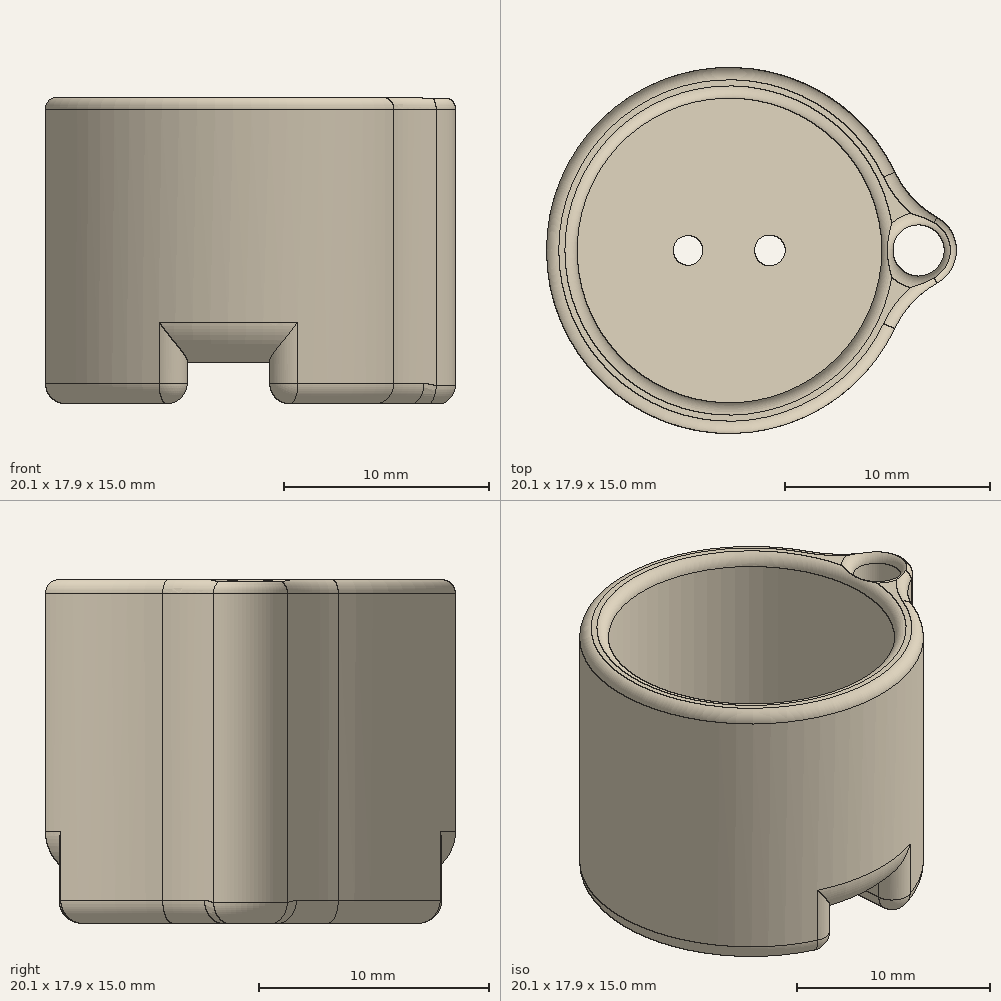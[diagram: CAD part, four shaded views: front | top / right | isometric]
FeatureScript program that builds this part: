
annotation { "Feature Type Name" : "Feature", "Feature Type Description" : "" }
export const myFeature = defineFeature(function(context is Context, id is Id, definition is map)
    precondition{}
    {
        {
            var Q0;
            Q0=qCreatedBy(makeId("Top.planeOp"),FACE);
            var sketch = newSketch(context, id + "F0", { "sketchPlane" : qUnion([Q0])});
            skCircle(sketch, "E0", {"center": v(0, 0) * mm, "radius": 7.45 * mm});
            skCircle(sketch, "E1", {"center": v(9.25, 0) * mm, "radius": 1.25 * mm});
            skArc(sketch, "E2.0", {"start": v(8.09, 3.83) * mm, "mid": v(-8.95, 0) * mm, "end": v(8.09, -3.83) * mm});
            skArc(sketch, "E3.0", {"start": v(10.16, -1.61) * mm, "mid": v(11.1, 0) * mm, "end": v(10.16, 1.61) * mm});
            skPoint(sketch, "E4.visualSharp", {"position": v(8.77, 1.79) * mm});
            skArc(sketch, "E4.filletArc", {"start": v(8.09, 3.83) * mm, "mid": v(8.95, 2.56) * mm, "end": v(10.16, 1.61) * mm});
            skPoint(sketch, "E5.visualSharp", {"position": v(8.77, -1.79) * mm});
            skArc(sketch, "E5.filletArc", {"start": v(10.16, -1.61) * mm, "mid": v(8.95, -2.56) * mm, "end": v(8.09, -3.83) * mm});
            skSolve(sketch);
        }
        {
            var Q0;
            Q0=makeQuery(id+"F0.imprint","IMPRINT",FACE,{"disambiguationData":[TD([[makeQuery(id+"F0.imprint","IMPRINT",EDGE,{"derivedFrom":sQuery(id+"F0.wireOp",EDGE,"E2.0")}),1.0]])]});
            extrude(context, id + "F1", {"entities" : qUnion([Q0]), "depth" : 15 * mm});
        }
        {
            var Q0;
            Q0=makeQuery(id+"F0.imprint","IMPRINT",FACE,{"disambiguationData":[TD([[makeQuery(id+"F0.imprint","IMPRINT",EDGE,{"derivedFrom":sQuery(id+"F0.wireOp",EDGE,"E0")}),1.0]])]});
            extrude(context, id + "F2", {"entities" : qUnion([Q0]), "operationType" : NewBodyOperationType.ADD, "depth" : 3 * mm});
        }
        {
            var Q0;
            Q0=makeQuery(id+"F1.opExtrude","CAP_FACE",FACE,{"disambiguationData":[OSD([sQuery(id+"F0.wireOp",EDGE,"E0"),sQuery(id+"F0.wireOp",EDGE,"E1"),sQuery(id+"F0.wireOp",EDGE,"E2.0"),sQuery(id+"F0.wireOp",EDGE,"E3.0"),sQuery(id+"F0.wireOp",EDGE,"E4.filletArc"),sQuery(id+"F0.wireOp",EDGE,"E5.filletArc")])],"isStart":false});
            fillet(context, id + "F3", {"entities" : qUnion([Q0]), "radius" : 0.6 * mm, "tangentPropagation" : true, "allowEdgeOverflow" : false});
        }
        {
            var Q0;
            Q0=makeQuery(id+"F0.imprint","IMPRINT",FACE,{"disambiguationData":[TD([[makeQuery(id+"F0.imprint","IMPRINT",EDGE,{"derivedFrom":sQuery(id+"F0.wireOp",EDGE,"E0")}),1.0]])]});
            var sketch = newSketch(context, id + "F4", { "sketchPlane" : qUnion([Q0])});
            skLineSegment(sketch, "E6.bottom", {"start": v(8.59, 1.11) * mm, "end": v(-5.98, 1.11) * mm});
            skLineSegment(sketch, "E6.top", {"start": v(8.59, -1.15) * mm, "end": v(-5.98, -1.15) * mm});
            skLineSegment(sketch, "E6.left", {"start": v(8.59, 1.11) * mm, "end": v(8.59, -1.15) * mm});
            skLineSegment(sketch, "E6.right", {"start": v(-5.98, 1.11) * mm, "end": v(-5.98, -1.15) * mm});
            skLineSegment(sketch, "E7", {"start": v(-2.02, -9.27) * mm, "end": v(-2.02, 9.18) * mm});
            skLineSegment(sketch, "E8.MirrorCS", {"start": v(2.02, -9.27) * mm, "end": v(2.02, 9.18) * mm});
            skLineSegment(sketch, "E9", {"start": v(-2.02, -9.27) * mm, "end": v(2.02, -9.27) * mm});
            skLineSegment(sketch, "E10", {"start": v(-2.02, 9.18) * mm, "end": v(2.02, 9.18) * mm});
            skSolve(sketch);
        }
        {
            var Q0;
            Q0 = qSketchRegion(id + "F4", true);
            extrude(context, id + "F5", {"entities" : qUnion([Q0]), "operationType" : NewBodyOperationType.REMOVE, "depth" : 2 * mm});
        }
        {
            var Q0;
            {var subQ0=sQuery(id+"F4.wireOp",EDGE,"E8.MirrorCS");Q0=makeQuery(id+"F5.boolean.opBoolean","COPY",EDGE,{"derivedFrom":makeQuery(id+"F5.opExtrude","CAP_EDGE",EDGE,{"disambiguationData":[OSD([subQ0]),TDD([makeQuery(id+"F4.imprint","IMPRINT",EDGE,{"disambiguationData":[TD([[makeQuery(id+"F4.imprint","INTERSECT",VERTEX,{"derivedFrom":[subQ0,sQuery(id+"F4.wireOp",EDGE,"E9")]}),-1.0]])],"derivedFrom":subQ0}),makeQuery(id+"F4.imprint","IMPRINT",EDGE,{"disambiguationData":[TD([[makeQuery(id+"F4.imprint","INTERSECT",VERTEX,{"derivedFrom":[sQuery(id+"F4.wireOp",EDGE,"E6.top"),subQ0]}),1.0]])],"derivedFrom":subQ0})])],"isStart":true})});}
            var Q1;
            {var subQ0=sQuery(id+"F4.wireOp",EDGE,"E7");Q1=makeQuery(id+"F5.boolean.opBoolean","COPY",EDGE,{"derivedFrom":makeQuery(id+"F5.opExtrude","CAP_EDGE",EDGE,{"disambiguationData":[OSD([subQ0]),TDD([makeQuery(id+"F4.imprint","IMPRINT",EDGE,{"disambiguationData":[TD([[makeQuery(id+"F4.imprint","INTERSECT",VERTEX,{"derivedFrom":[subQ0,sQuery(id+"F4.wireOp",EDGE,"E9")]}),-1.0]])],"derivedFrom":subQ0}),makeQuery(id+"F4.imprint","IMPRINT",EDGE,{"disambiguationData":[TD([[makeQuery(id+"F4.imprint","INTERSECT",VERTEX,{"derivedFrom":[sQuery(id+"F4.wireOp",EDGE,"E6.top"),subQ0]}),1.0]])],"derivedFrom":subQ0})])],"isStart":true})});}
            var Q2;
            {var subQ0=sQuery(id+"F4.wireOp",EDGE,"E7");Q2=makeQuery(id+"F5.boolean.opBoolean","COPY",EDGE,{"derivedFrom":makeQuery(id+"F5.opExtrude","CAP_EDGE",EDGE,{"disambiguationData":[OSD([subQ0]),TDD([makeQuery(id+"F4.imprint","IMPRINT",EDGE,{"disambiguationData":[TD([[makeQuery(id+"F4.imprint","INTERSECT",VERTEX,{"derivedFrom":[sQuery(id+"F4.wireOp",EDGE,"E6.bottom"),subQ0]}),-1.0]])],"derivedFrom":subQ0}),makeQuery(id+"F4.imprint","IMPRINT",EDGE,{"disambiguationData":[TD([[makeQuery(id+"F4.imprint","INTERSECT",VERTEX,{"derivedFrom":[subQ0,sQuery(id+"F4.wireOp",EDGE,"E10")]}),1.0]])],"derivedFrom":subQ0})])],"isStart":true})});}
            var Q3;
            {var subQ0=sQuery(id+"F4.wireOp",EDGE,"E8.MirrorCS");Q3=makeQuery(id+"F5.boolean.opBoolean","COPY",EDGE,{"derivedFrom":makeQuery(id+"F5.opExtrude","CAP_EDGE",EDGE,{"disambiguationData":[OSD([subQ0]),TDD([makeQuery(id+"F4.imprint","IMPRINT",EDGE,{"disambiguationData":[TD([[makeQuery(id+"F4.imprint","INTERSECT",VERTEX,{"derivedFrom":[sQuery(id+"F4.wireOp",EDGE,"E6.bottom"),subQ0]}),-1.0]])],"derivedFrom":subQ0}),makeQuery(id+"F4.imprint","IMPRINT",EDGE,{"disambiguationData":[TD([[makeQuery(id+"F4.imprint","INTERSECT",VERTEX,{"derivedFrom":[subQ0,sQuery(id+"F4.wireOp",EDGE,"E10")]}),1.0]])],"derivedFrom":subQ0})])],"isStart":true})});}
            var Q4;
            {var subQ1=sQuery(id+"F0.wireOp",EDGE,"E2.0");var subQ2=sQuery(id+"F4.wireOp",EDGE,"E7");Q4=makeQuery(id+"F5.boolean.opBoolean","SPLIT",EDGE,{"disambiguationData":[TD([makeQuery(id+"F5.opExtrude","SWEPT_FACE",FACE,{"disambiguationData":[OSD([subQ2]),TDD([makeQuery(id+"F4.imprint","IMPRINT",EDGE,{"disambiguationData":[TD([[makeQuery(id+"F4.imprint","INTERSECT",VERTEX,{"derivedFrom":[subQ2,sQuery(id+"F4.wireOp",EDGE,"E9")]}),-1.0]])],"derivedFrom":subQ2}),makeQuery(id+"F4.imprint","IMPRINT",EDGE,{"disambiguationData":[TD([[makeQuery(id+"F4.imprint","INTERSECT",VERTEX,{"derivedFrom":[sQuery(id+"F4.wireOp",EDGE,"E6.top"),subQ2]}),1.0]])],"derivedFrom":subQ2})])]})])],"derivedFrom":makeQuery(id+"F1.opExtrude","CAP_EDGE",EDGE,{"disambiguationData":[OSD([subQ1])],"isStart":true})});}
            var Q5;
            {var subQ0=sQuery(id+"F0.wireOp",EDGE,"E5.filletArc");var subQ2=sQuery(id+"F0.wireOp",EDGE,"E2.0");Q5=makeQuery(id+"F5.boolean.opBoolean","SPLIT",EDGE,{"disambiguationData":[TD([makeQuery(id+"F1.opExtrude","SWEPT_FACE",FACE,{"disambiguationData":[OSD([subQ0])]})])],"derivedFrom":makeQuery(id+"F1.opExtrude","CAP_EDGE",EDGE,{"disambiguationData":[OSD([subQ2])],"isStart":true})});}
            fillet(context, id + "F6", {"entities" : qUnion([Q0, Q1, Q2, Q3, Q4, Q5]), "radius" : 1 * mm, "tangentPropagation" : true, "allowEdgeOverflow" : false});
        }
        {
            var Q0;
            Q0=makeQuery(id+"F0.imprint","IMPRINT",FACE,{"disambiguationData":[TD([[makeQuery(id+"F0.imprint","IMPRINT",EDGE,{"derivedFrom":sQuery(id+"F0.wireOp",EDGE,"E0")}),1.0]])]});
            var sketch = newSketch(context, id + "F7", { "sketchPlane" : qUnion([Q0])});
            skCircle(sketch, "E11", {"center": v(-2.02, 0) * mm, "radius": 0.72 * mm});
            skCircle(sketch, "E12", {"center": v(1.98, 0) * mm, "radius": 0.75 * mm});
            skSolve(sketch);
        }
        {
            var Q0;
            Q0 = qSketchRegion(id + "F7", true);
            extrude(context, id + "F8", {"entities" : qUnion([Q0]), "operationType" : NewBodyOperationType.REMOVE, "depth" : 25 * mm});
        }
        {
            var Q0;
            Q0=makeQuery(id+"F8.boolean.opBoolean","INTERSECT",EDGE,{"derivedFrom":[makeQuery(id+"F5.boolean.opBoolean","COPY",FACE,{"derivedFrom":makeQuery(id+"F5.opExtrude","CAP_FACE",FACE,{"disambiguationData":[OSD([sQuery(id+"F4.wireOp",EDGE,"E6.bottom"),sQuery(id+"F4.wireOp",EDGE,"E6.top"),sQuery(id+"F4.wireOp",EDGE,"E6.left"),sQuery(id+"F4.wireOp",EDGE,"E6.right"),sQuery(id+"F4.wireOp",EDGE,"E7"),sQuery(id+"F4.wireOp",EDGE,"E8.MirrorCS"),sQuery(id+"F4.wireOp",EDGE,"E9"),sQuery(id+"F4.wireOp",EDGE,"E10")])],"isStart":false})}),makeQuery(id+"F8.opExtrude","SWEPT_FACE",FACE,{"disambiguationData":[OSD([sQuery(id+"F7.wireOp",EDGE,"E12")])]})]});
            var Q1;
            Q1=makeQuery(id+"F8.boolean.opBoolean","INTERSECT",EDGE,{"derivedFrom":[makeQuery(id+"F5.boolean.opBoolean","COPY",FACE,{"derivedFrom":makeQuery(id+"F5.opExtrude","CAP_FACE",FACE,{"disambiguationData":[OSD([sQuery(id+"F4.wireOp",EDGE,"E6.bottom"),sQuery(id+"F4.wireOp",EDGE,"E6.top"),sQuery(id+"F4.wireOp",EDGE,"E6.left"),sQuery(id+"F4.wireOp",EDGE,"E6.right"),sQuery(id+"F4.wireOp",EDGE,"E7"),sQuery(id+"F4.wireOp",EDGE,"E8.MirrorCS"),sQuery(id+"F4.wireOp",EDGE,"E9"),sQuery(id+"F4.wireOp",EDGE,"E10")])],"isStart":false})}),makeQuery(id+"F8.opExtrude","SWEPT_FACE",FACE,{"disambiguationData":[OSD([sQuery(id+"F7.wireOp",EDGE,"E11")])]})]});
            var Q2;
            Q2=makeQuery(id+"F5.boolean.opBoolean","INTERSECT",EDGE,{"derivedFrom":[makeQuery(id+"F1.opExtrude","SWEPT_FACE",FACE,{"disambiguationData":[OSD([sQuery(id+"F0.wireOp",EDGE,"E1")])]}),makeQuery(id+"F5.opExtrude","CAP_FACE",FACE,{"disambiguationData":[OSD([sQuery(id+"F4.wireOp",EDGE,"E6.bottom"),sQuery(id+"F4.wireOp",EDGE,"E6.top"),sQuery(id+"F4.wireOp",EDGE,"E6.left"),sQuery(id+"F4.wireOp",EDGE,"E6.right"),sQuery(id+"F4.wireOp",EDGE,"E7"),sQuery(id+"F4.wireOp",EDGE,"E8.MirrorCS"),sQuery(id+"F4.wireOp",EDGE,"E9"),sQuery(id+"F4.wireOp",EDGE,"E10")])],"isStart":false})]});
            fillet(context, id + "F9", {"entities" : qUnion([Q0, Q1, Q2]), "radius" : 0.8 * mm, "tangentPropagation" : true, "allowEdgeOverflow" : false});
        }
        {
            var Q0;
            Q0=makeQuery(id+"F5.boolean.opBoolean","INTERSECT",EDGE,{"disambiguationData":[OD(0.0)],"derivedFrom":[makeQuery(id+"F1.opExtrude","SWEPT_FACE",FACE,{"disambiguationData":[OSD([sQuery(id+"F0.wireOp",EDGE,"E2.0")])]}),makeQuery(id+"F5.opExtrude","CAP_FACE",FACE,{"disambiguationData":[OSD([sQuery(id+"F4.wireOp",EDGE,"E6.bottom"),sQuery(id+"F4.wireOp",EDGE,"E6.top"),sQuery(id+"F4.wireOp",EDGE,"E6.left"),sQuery(id+"F4.wireOp",EDGE,"E6.right"),sQuery(id+"F4.wireOp",EDGE,"E7"),sQuery(id+"F4.wireOp",EDGE,"E8.MirrorCS"),sQuery(id+"F4.wireOp",EDGE,"E9"),sQuery(id+"F4.wireOp",EDGE,"E10")])],"isStart":false})]});
            var Q1;
            Q1=makeQuery(id+"F5.boolean.opBoolean","INTERSECT",EDGE,{"disambiguationData":[OD(1.0)],"derivedFrom":[makeQuery(id+"F1.opExtrude","SWEPT_FACE",FACE,{"disambiguationData":[OSD([sQuery(id+"F0.wireOp",EDGE,"E2.0")])]}),makeQuery(id+"F5.opExtrude","CAP_FACE",FACE,{"disambiguationData":[OSD([sQuery(id+"F4.wireOp",EDGE,"E6.bottom"),sQuery(id+"F4.wireOp",EDGE,"E6.top"),sQuery(id+"F4.wireOp",EDGE,"E6.left"),sQuery(id+"F4.wireOp",EDGE,"E6.right"),sQuery(id+"F4.wireOp",EDGE,"E7"),sQuery(id+"F4.wireOp",EDGE,"E8.MirrorCS"),sQuery(id+"F4.wireOp",EDGE,"E9"),sQuery(id+"F4.wireOp",EDGE,"E10")])],"isStart":false})]});
            fillet(context, id + "F10", {"entities" : qUnion([Q0, Q1]), "radius" : 2 * mm, "tangentPropagation" : true, "allowEdgeOverflow" : false});
        }
        {
            var Q0;
            {var subQ0=sQuery(id+"F4.wireOp",EDGE,"E7");Q0=makeQuery(id+"F5.boolean.opBoolean","INTERSECT",EDGE,{"derivedFrom":[makeQuery(id+"F1.opExtrude","SWEPT_FACE",FACE,{"disambiguationData":[OSD([sQuery(id+"F0.wireOp",EDGE,"E2.0")])]}),makeQuery(id+"F5.opExtrude","SWEPT_FACE",FACE,{"disambiguationData":[OSD([subQ0]),TDD([makeQuery(id+"F4.imprint","IMPRINT",EDGE,{"disambiguationData":[TD([[makeQuery(id+"F4.imprint","INTERSECT",VERTEX,{"derivedFrom":[sQuery(id+"F4.wireOp",EDGE,"E6.bottom"),subQ0]}),-1.0]])],"derivedFrom":subQ0}),makeQuery(id+"F4.imprint","IMPRINT",EDGE,{"disambiguationData":[TD([[makeQuery(id+"F4.imprint","INTERSECT",VERTEX,{"derivedFrom":[subQ0,sQuery(id+"F4.wireOp",EDGE,"E10")]}),1.0]])],"derivedFrom":subQ0})])]})]});}
            var Q1;
            {var subQ0=sQuery(id+"F4.wireOp",EDGE,"E8.MirrorCS");Q1=makeQuery(id+"F5.boolean.opBoolean","INTERSECT",EDGE,{"derivedFrom":[makeQuery(id+"F1.opExtrude","SWEPT_FACE",FACE,{"disambiguationData":[OSD([sQuery(id+"F0.wireOp",EDGE,"E2.0")])]}),makeQuery(id+"F5.opExtrude","SWEPT_FACE",FACE,{"disambiguationData":[OSD([subQ0]),TDD([makeQuery(id+"F4.imprint","IMPRINT",EDGE,{"disambiguationData":[TD([[makeQuery(id+"F4.imprint","INTERSECT",VERTEX,{"derivedFrom":[sQuery(id+"F4.wireOp",EDGE,"E6.bottom"),subQ0]}),-1.0]])],"derivedFrom":subQ0}),makeQuery(id+"F4.imprint","IMPRINT",EDGE,{"disambiguationData":[TD([[makeQuery(id+"F4.imprint","INTERSECT",VERTEX,{"derivedFrom":[subQ0,sQuery(id+"F4.wireOp",EDGE,"E10")]}),1.0]])],"derivedFrom":subQ0})])]})]});}
            var Q2;
            {var subQ0=sQuery(id+"F4.wireOp",EDGE,"E8.MirrorCS");Q2=makeQuery(id+"F5.boolean.opBoolean","INTERSECT",EDGE,{"derivedFrom":[makeQuery(id+"F1.opExtrude","SWEPT_FACE",FACE,{"disambiguationData":[OSD([sQuery(id+"F0.wireOp",EDGE,"E2.0")])]}),makeQuery(id+"F5.opExtrude","SWEPT_FACE",FACE,{"disambiguationData":[OSD([subQ0]),TDD([makeQuery(id+"F4.imprint","IMPRINT",EDGE,{"disambiguationData":[TD([[makeQuery(id+"F4.imprint","INTERSECT",VERTEX,{"derivedFrom":[subQ0,sQuery(id+"F4.wireOp",EDGE,"E9")]}),-1.0]])],"derivedFrom":subQ0}),makeQuery(id+"F4.imprint","IMPRINT",EDGE,{"disambiguationData":[TD([[makeQuery(id+"F4.imprint","INTERSECT",VERTEX,{"derivedFrom":[sQuery(id+"F4.wireOp",EDGE,"E6.top"),subQ0]}),1.0]])],"derivedFrom":subQ0})])]})]});}
            var Q3;
            {var subQ0=sQuery(id+"F4.wireOp",EDGE,"E7");Q3=makeQuery(id+"F5.boolean.opBoolean","INTERSECT",EDGE,{"derivedFrom":[makeQuery(id+"F1.opExtrude","SWEPT_FACE",FACE,{"disambiguationData":[OSD([sQuery(id+"F0.wireOp",EDGE,"E2.0")])]}),makeQuery(id+"F5.opExtrude","SWEPT_FACE",FACE,{"disambiguationData":[OSD([subQ0]),TDD([makeQuery(id+"F4.imprint","IMPRINT",EDGE,{"disambiguationData":[TD([[makeQuery(id+"F4.imprint","INTERSECT",VERTEX,{"derivedFrom":[subQ0,sQuery(id+"F4.wireOp",EDGE,"E9")]}),-1.0]])],"derivedFrom":subQ0}),makeQuery(id+"F4.imprint","IMPRINT",EDGE,{"disambiguationData":[TD([[makeQuery(id+"F4.imprint","INTERSECT",VERTEX,{"derivedFrom":[sQuery(id+"F4.wireOp",EDGE,"E6.top"),subQ0]}),1.0]])],"derivedFrom":subQ0})])]})]});}
            fillet(context, id + "F11", {"entities" : qUnion([Q0, Q1, Q2, Q3]), "radius" : 1 * mm, "tangentPropagation" : true, "allowEdgeOverflow" : false});
        }
    });
